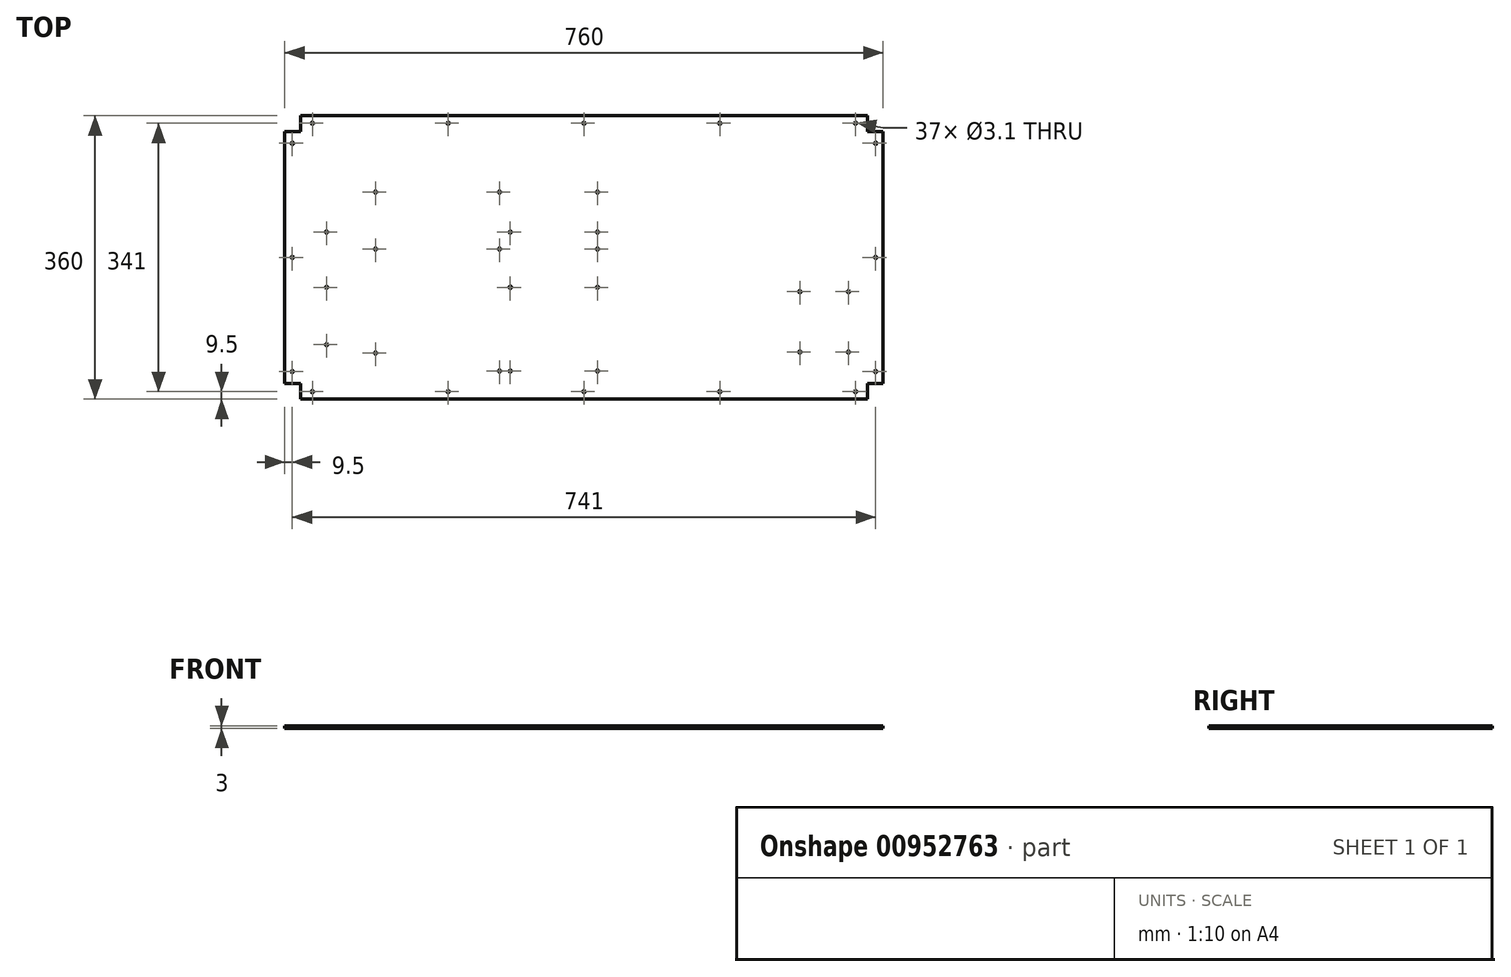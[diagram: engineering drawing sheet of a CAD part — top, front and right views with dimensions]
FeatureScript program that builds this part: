
annotation { "Feature Type Name" : "Feature", "Feature Type Description" : "" }
export const myFeature = defineFeature(function(context is Context, id is Id, definition is map)
    precondition{}
    {
        {
            var Q0;
            Q0=qCreatedBy(makeId("Top.planeOp"),FACE);
            var sketch = newSketch(context, id + "F0", { "sketchPlane" : qUnion([Q0])});
            skLineSegment(sketch, "E0.bottom", {"start": v(-380, -180) * mm, "end": v(380, -180) * mm});
            skLineSegment(sketch, "E0.top", {"start": v(-380, 180) * mm, "end": v(380, 180) * mm});
            skLineSegment(sketch, "E0.left", {"start": v(-380, -180) * mm, "end": v(-380, 180) * mm});
            skLineSegment(sketch, "E0.right", {"start": v(380, -180) * mm, "end": v(380, 180) * mm});
            skPoint(sketch, "E0.middle", {"position": v(0, 0) * mm});
            skSolve(sketch);
        }
        {
            var Q0;
            Q0=makeQuery(id+"F0.imprint","IMPRINT",FACE,{"disambiguationData":[TD([[makeQuery(id+"F0.imprint","IMPRINT",EDGE,{"derivedFrom":sQuery(id+"F0.wireOp",EDGE,"E0.bottom")}),1.0]])]});
            extrude(context, id + "F1", {"entities" : qUnion([Q0]), "endBound" : BoundingType.SYMMETRIC, "depth" : 3 * mm, "offsetDistance" : 25 * mm});
        }
        {
            var Q0;
            Q0=makeQuery(id+"F1.opExtrude","CAP_FACE",FACE,{"disambiguationData":[OSD([sQuery(id+"F0.wireOp",EDGE,"E0.bottom"),sQuery(id+"F0.wireOp",EDGE,"E0.top"),sQuery(id+"F0.wireOp",EDGE,"E0.left"),sQuery(id+"F0.wireOp",EDGE,"E0.right")])],"isStart":false});
            var sketch = newSketch(context, id + "F2", { "sketchPlane" : qUnion([Q0])});
            skLineSegment(sketch, "E1.bottom", {"start": v(-380, -180) * mm, "end": v(-360, -180) * mm});
            skLineSegment(sketch, "E1.top", {"start": v(-380, -160) * mm, "end": v(-360, -160) * mm});
            skLineSegment(sketch, "E1.left", {"start": v(-380, -180) * mm, "end": v(-380, -160) * mm});
            skLineSegment(sketch, "E1.right", {"start": v(-360, -180) * mm, "end": v(-360, -160) * mm});
            skLineSegment(sketch, "E2.bottom", {"start": v(380, -180) * mm, "end": v(360, -180) * mm});
            skLineSegment(sketch, "E2.top", {"start": v(380, -160) * mm, "end": v(360, -160) * mm});
            skLineSegment(sketch, "E2.left", {"start": v(380, -180) * mm, "end": v(380, -160) * mm});
            skLineSegment(sketch, "E2.right", {"start": v(360, -180) * mm, "end": v(360, -160) * mm});
            skLineSegment(sketch, "E3.bottom", {"start": v(380, 180) * mm, "end": v(360, 180) * mm});
            skLineSegment(sketch, "E3.top", {"start": v(380, 160) * mm, "end": v(360, 160) * mm});
            skLineSegment(sketch, "E3.left", {"start": v(380, 180) * mm, "end": v(380, 160) * mm});
            skLineSegment(sketch, "E3.right", {"start": v(360, 180) * mm, "end": v(360, 160) * mm});
            skLineSegment(sketch, "E4.bottom", {"start": v(-380, 180) * mm, "end": v(-360, 180) * mm});
            skLineSegment(sketch, "E4.top", {"start": v(-380, 160) * mm, "end": v(-360, 160) * mm});
            skLineSegment(sketch, "E4.left", {"start": v(-380, 180) * mm, "end": v(-380, 160) * mm});
            skLineSegment(sketch, "E4.right", {"start": v(-360, 180) * mm, "end": v(-360, 160) * mm});
            skSolve(sketch);
        }
        {
            var Q0;
            Q0=makeQuery(id+"F2.imprint","IMPRINT",FACE,{"disambiguationData":[TD([[makeQuery(id+"F2.imprint","IMPRINT",EDGE,{"derivedFrom":sQuery(id+"F2.wireOp",EDGE,"E1.bottom")}),1.0]])]});
            var Q1;
            Q1=makeQuery(id+"F2.imprint","IMPRINT",FACE,{"disambiguationData":[TD([[makeQuery(id+"F2.imprint","IMPRINT",EDGE,{"derivedFrom":sQuery(id+"F2.wireOp",EDGE,"E4.bottom")}),-1.0]])]});
            var Q2;
            Q2=makeQuery(id+"F2.imprint","IMPRINT",FACE,{"disambiguationData":[TD([[makeQuery(id+"F2.imprint","IMPRINT",EDGE,{"derivedFrom":sQuery(id+"F2.wireOp",EDGE,"E2.bottom")}),1.0]])]});
            var Q3;
            Q3=makeQuery(id+"F2.imprint","IMPRINT",FACE,{"disambiguationData":[TD([[makeQuery(id+"F2.imprint","IMPRINT",EDGE,{"derivedFrom":sQuery(id+"F2.wireOp",EDGE,"E3.bottom")}),-1.0]])]});
            extrude(context, id + "F3", {"entities" : qUnion([Q0, Q1, Q2, Q3]), "operationType" : NewBodyOperationType.REMOVE, "endBound" : BoundingType.THROUGH_ALL, "oppositeDirection" : true, "depth" : 25 * mm, "offsetDistance" : 25 * mm});
        }
        {
            var Q0;
            Q0=makeQuery(id+"F1.opExtrude","CAP_FACE",FACE,{"disambiguationData":[OSD([sQuery(id+"F0.wireOp",EDGE,"E0.bottom"),sQuery(id+"F0.wireOp",EDGE,"E0.top"),sQuery(id+"F0.wireOp",EDGE,"E0.left"),sQuery(id+"F0.wireOp",EDGE,"E0.right")])],"isStart":false});
            var sketch = newSketch(context, id + "F4", { "sketchPlane" : qUnion([Q0])});
            skLineSegment(sketch, "E5.bottom", {"start": v(-346.39, 47.63) * mm, "end": v(40, 47.63) * mm, "construction": true});
            skLineSegment(sketch, "E5.top", {"start": v(-346.39, -160) * mm, "end": v(40, -160) * mm, "construction": true});
            skLineSegment(sketch, "E5.left", {"start": v(-346.39, 47.63) * mm, "end": v(-346.39, -160) * mm, "construction": true});
            skLineSegment(sketch, "E5.right", {"start": v(40, 47.63) * mm, "end": v(40, -160) * mm, "construction": true});
            skCircle(sketch, "E6", {"center": v(17.2, 32.19) * mm, "radius": 1.55 * mm});
            skCircle(sketch, "E7", {"center": v(-93.65, 32.19) * mm, "radius": 1.55 * mm});
            skCircle(sketch, "E8", {"center": v(-327, 32.19) * mm, "radius": 1.55 * mm});
            skCircle(sketch, "E9", {"center": v(17.2, -144.34) * mm, "radius": 1.55 * mm});
            skCircle(sketch, "E10", {"center": v(-93.65, -144.34) * mm, "radius": 1.55 * mm});
            skCircle(sketch, "E11", {"center": v(-327, -110.84) * mm, "radius": 1.55 * mm});
            skCircle(sketch, "E12", {"center": v(-327, -37.96) * mm, "radius": 1.55 * mm});
            skCircle(sketch, "E13", {"center": v(-93.65, -37.96) * mm, "radius": 1.55 * mm});
            skCircle(sketch, "E14", {"center": v(17.2, -37.96) * mm, "radius": 1.55 * mm});
            skLineSegment(sketch, "E15.bottom", {"start": v(60, 0) * mm, "end": v(210, 0) * mm, "construction": true});
            skLineSegment(sketch, "E15.top", {"start": v(60, -180) * mm, "end": v(210, -180) * mm});
            skLineSegment(sketch, "E15.left", {"start": v(60, 0) * mm, "end": v(60, -180) * mm, "construction": true});
            skLineSegment(sketch, "E15.right", {"start": v(210, 0) * mm, "end": v(210, -180) * mm, "construction": true});
            skLineSegment(sketch, "E16.bottom", {"start": v(270.15, -29.55) * mm, "end": v(340, -29.55) * mm, "construction": true});
            skLineSegment(sketch, "E16.top", {"start": v(270.15, -130) * mm, "end": v(340, -130) * mm, "construction": true});
            skLineSegment(sketch, "E16.left", {"start": v(270.15, -29.55) * mm, "end": v(270.15, -130) * mm, "construction": true});
            skLineSegment(sketch, "E16.right", {"start": v(340, -29.55) * mm, "end": v(340, -130) * mm, "construction": true});
            skCircle(sketch, "E17", {"center": v(274.21, -43.55) * mm, "radius": 1.55 * mm});
            skCircle(sketch, "E18", {"center": v(335.94, -43.55) * mm, "radius": 1.55 * mm});
            skCircle(sketch, "E19", {"center": v(274.21, -120.15) * mm, "radius": 1.55 * mm});
            skCircle(sketch, "E20", {"center": v(335.94, -120.15) * mm, "radius": 1.55 * mm});
            skCircle(sketch, "E21", {"center": v(-264.75, -121.48) * mm, "radius": 1.55 * mm});
            skCircle(sketch, "E22", {"center": v(-107.27, 10.6) * mm, "radius": 1.55 * mm});
            skCircle(sketch, "E23", {"center": v(17.2, 10.6) * mm, "radius": 1.55 * mm});
            skCircle(sketch, "E24", {"center": v(-107.27, 82.98) * mm, "radius": 1.55 * mm});
            skCircle(sketch, "E25", {"center": v(17.2, 82.98) * mm, "radius": 1.55 * mm});
            skCircle(sketch, "E26", {"center": v(-107.27, -144.34) * mm, "radius": 1.55 * mm});
            skCircle(sketch, "E27", {"center": v(-264.75, 10.6) * mm, "radius": 1.55 * mm});
            skCircle(sketch, "E28", {"center": v(-264.75, 82.98) * mm, "radius": 1.55 * mm});
            skSolve(sketch);
        }
        {
            var Q0;
            Q0 = qSketchRegion(id + "F4", true);
            extrude(context, id + "F5", {"entities" : qUnion([Q0]), "operationType" : NewBodyOperationType.REMOVE, "endBound" : BoundingType.THROUGH_ALL, "oppositeDirection" : true, "depth" : 25 * mm, "offsetDistance" : 25 * mm});
        }
        {
            var Q0;
            Q0=makeQuery(id+"F1.opExtrude","CAP_FACE",FACE,{"disambiguationData":[OSD([sQuery(id+"F0.wireOp",EDGE,"E0.bottom"),sQuery(id+"F0.wireOp",EDGE,"E0.top"),sQuery(id+"F0.wireOp",EDGE,"E0.left"),sQuery(id+"F0.wireOp",EDGE,"E0.right")])],"isStart":false});
            var sketch = newSketch(context, id + "F6", { "sketchPlane" : qUnion([Q0])});
            skCircle(sketch, "E29", {"center": v(-370.5, 145) * mm, "radius": 1.55 * mm});
            skCircle(sketch, "E30", {"center": v(-370.5, 0) * mm, "radius": 1.55 * mm});
            skCircle(sketch, "E31", {"center": v(-370.5, -145) * mm, "radius": 1.55 * mm});
            skCircle(sketch, "E32", {"center": v(370.5, -145) * mm, "radius": 1.55 * mm});
            skCircle(sketch, "E33", {"center": v(370.5, 0) * mm, "radius": 1.55 * mm});
            skCircle(sketch, "E34", {"center": v(370.5, 145) * mm, "radius": 1.55 * mm});
            skCircle(sketch, "E35", {"center": v(0, 170.5) * mm, "radius": 1.55 * mm});
            skCircle(sketch, "E36", {"center": v(172.5, 170.5) * mm, "radius": 1.55 * mm});
            skCircle(sketch, "E37", {"center": v(345, 170.5) * mm, "radius": 1.55 * mm});
            skCircle(sketch, "E38", {"center": v(-172.5, 170.5) * mm, "radius": 1.55 * mm});
            skCircle(sketch, "E39", {"center": v(-345, 170.5) * mm, "radius": 1.55 * mm});
            skCircle(sketch, "E40", {"center": v(-345, -170.5) * mm, "radius": 1.55 * mm});
            skCircle(sketch, "E41", {"center": v(-172.5, -170.5) * mm, "radius": 1.55 * mm});
            skCircle(sketch, "E42", {"center": v(0, -170.5) * mm, "radius": 1.55 * mm});
            skCircle(sketch, "E43", {"center": v(172.5, -170.5) * mm, "radius": 1.55 * mm});
            skCircle(sketch, "E44", {"center": v(345, -170.5) * mm, "radius": 1.55 * mm});
            skLineSegment(sketch, "E45", {"start": v(-345, 170.5) * mm, "end": v(-172.5, 170.5) * mm, "construction": true});
            skLineSegment(sketch, "E46", {"start": v(-172.5, 170.5) * mm, "end": v(0, 170.5) * mm, "construction": true});
            skLineSegment(sketch, "E47", {"start": v(0, 170.5) * mm, "end": v(172.5, 170.5) * mm, "construction": true});
            skLineSegment(sketch, "E48", {"start": v(172.5, 170.5) * mm, "end": v(345, 170.5) * mm, "construction": true});
            skSolve(sketch);
        }
        {
            var Q0;
            Q0 = qSketchRegion(id + "F6", true);
            extrude(context, id + "F7", {"entities" : qUnion([Q0]), "operationType" : NewBodyOperationType.REMOVE, "endBound" : BoundingType.THROUGH_ALL, "oppositeDirection" : true, "depth" : 25 * mm, "offsetDistance" : 25 * mm});
        }
    });
